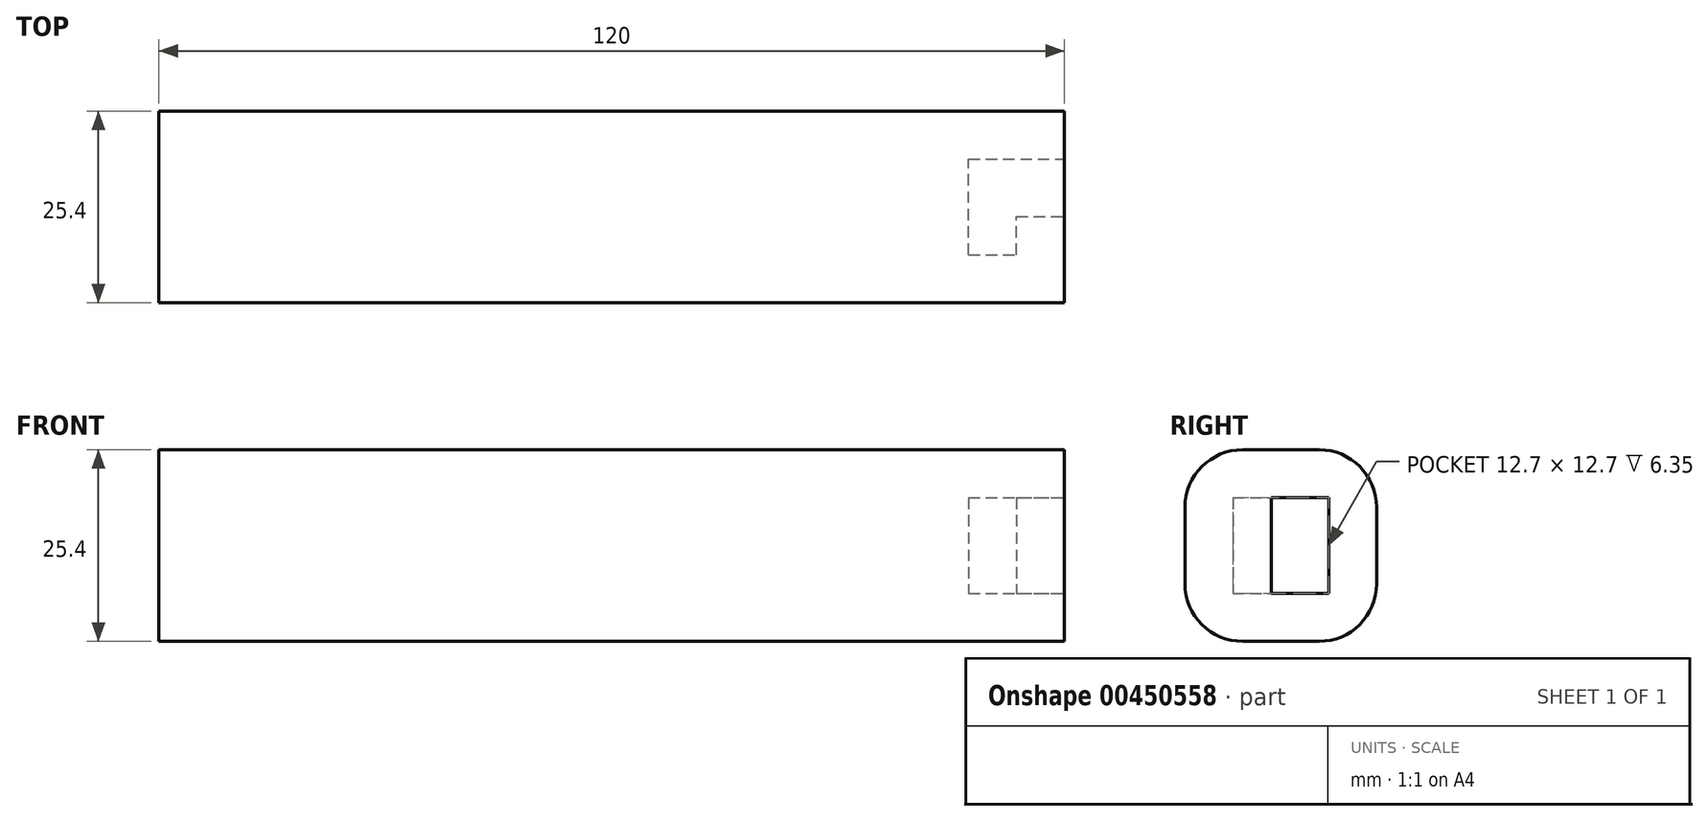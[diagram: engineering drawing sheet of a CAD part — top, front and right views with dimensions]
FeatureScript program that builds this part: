
annotation { "Feature Type Name" : "Feature", "Feature Type Description" : "" }
export const myFeature = defineFeature(function(context is Context, id is Id, definition is map)
    precondition{}
    {
        {
            var Q0;
            Q0=qCreatedBy(makeId("Top.planeOp"),FACE);
            var sketch = newSketch(context, id + "F0", { "sketchPlane" : qUnion([Q0])});
            skLineSegment(sketch, "E0.bottom", {"start": v(0, 0) * mm, "end": v(120, 0) * mm});
            skLineSegment(sketch, "E0.top", {"start": v(0, 25.4) * mm, "end": v(120, 25.4) * mm});
            skLineSegment(sketch, "E0.left", {"start": v(0, 0) * mm, "end": v(0, 25.4) * mm});
            skLineSegment(sketch, "E0.right", {"start": v(120, 0) * mm, "end": v(120, 25.4) * mm});
            skSolve(sketch);
        }
        {
            var Q0;
            Q0=makeQuery(id+"F0.imprint","IMPRINT",FACE,{"disambiguationData":[TD([[makeQuery(id+"F0.imprint","IMPRINT",EDGE,{"derivedFrom":sQuery(id+"F0.wireOp",EDGE,"E0.bottom")}),1.0]])]});
            extrude(context, id + "F1", {"entities" : qUnion([Q0]), "depth" : 25.4 * mm});
        }
        {
            var Q0;
            Q0=makeQuery(id+"F1.opExtrude","SWEPT_FACE",FACE,{"disambiguationData":[OSD([sQuery(id+"F0.wireOp",EDGE,"E0.right")])]});
            shell(context, id + "F2", {"entities" : qUnion([Q0]), "thickness" : 6.35 * mm});
        }
        {
            var Q0;
            Q0=makeQuery(id+"F1.opExtrude","SWEPT_FACE",FACE,{"disambiguationData":[OSD([sQuery(id+"F0.wireOp",EDGE,"E0.right")])]});
            var sketch = newSketch(context, id + "F3", { "sketchPlane" : qUnion([Q0])});
            skLineSegment(sketch, "E1", {"start": v(6.35, 19.05) * mm, "end": v(11.43, 19.05) * mm});
            skLineSegment(sketch, "E2", {"start": v(11.43, 19.05) * mm, "end": v(11.43, 6.35) * mm});
            skSolve(sketch);
        }
        {
            var Q0;
            Q0=makeQuery(id+"F3.imprint","IMPRINT",FACE,{"disambiguationData":[TD([[makeQuery(id+"F3.imprint","IMPRINT",EDGE,{"derivedFrom":sQuery(id+"F3.wireOp",EDGE,"E1")}),-1.0]])]});
            extrude(context, id + "F4", {"entities" : qUnion([Q0]), "operationType" : NewBodyOperationType.ADD, "oppositeDirection" : true, "depth" : 6.35 * mm});
        }
        {
            var Q0;
            Q0=makeQuery(id+"F2.opShell","OFFSET_FACE",FACE,{"disambiguationData":[OSD([sQuery(id+"F0.wireOp",EDGE,"E0.left")])]});
            extrude(context, id + "F5", {"entities" : qUnion([Q0]), "operationType" : NewBodyOperationType.ADD, "depth" : 100.95 * mm});
        }
        {
            var Q0;
            Q0=makeQuery(id+"F1.opExtrude","CAP_EDGE",EDGE,{"disambiguationData":[OSD([sQuery(id+"F0.wireOp",EDGE,"E0.top")])],"isStart":false});
            var Q1;
            Q1=makeQuery(id+"F1.opExtrude","CAP_EDGE",EDGE,{"disambiguationData":[OSD([sQuery(id+"F0.wireOp",EDGE,"E0.bottom")])],"isStart":false});
            var Q2;
            Q2=makeQuery(id+"F1.opExtrude","CAP_EDGE",EDGE,{"disambiguationData":[OSD([sQuery(id+"F0.wireOp",EDGE,"E0.bottom")])],"isStart":true});
            var Q3;
            Q3=makeQuery(id+"F1.opExtrude","CAP_EDGE",EDGE,{"disambiguationData":[OSD([sQuery(id+"F0.wireOp",EDGE,"E0.top")])],"isStart":true});
            fillet(context, id + "F6", {"entities" : qUnion([Q0, Q1, Q2, Q3]), "radius" : 7.62 * mm, "tangentPropagation" : true, "allowEdgeOverflow" : false});
        }
    });
